# Revit family: Plum Fix_Toilet_Argent_Grace BTW Toilet S&P Trap UNI ENTRY
name_source: partatom
category: Plumbing Fixtures
revit_build: Autodesk Revit 2016 (Build: 20150220_1215(x64)
units: mm (PartAtom-declared; Revit-internal decimal feet)

## family parameters
Always vertical = Yes
Cut with Voids When Loaded = No
OmniClass Number = 23.45.05.21.11
OmniClass Title = Water Closets
Part Type = Normal
Room Calculation Point = No
Round Connector Dimension = Use Diameter
Shared = No
Work Plane-Based = No

## types (1)
- S-Trap  - Rear Water Entry
    Angle Offset = 0 mm  [stored 0 ft]
    Body Material = z_Argent_Ceramic White
    CW Connection = Yes
    CWFU = 0
    Cost = 0 $
    Description = Grace Back-To-Wall Toilet Suite
    Flush Material = z_Argent_Chrome
    HW Connection = No
    HWFU = 0
    Manufacturer = Argent
    Manufacturer_Overall Depth = 620 mm  [stored 2.03412 ft]
    Manufacturer_Overall Height = 795 mm  [stored 2.60827 ft]
    Manufacturer_Overall Width = 380 mm
    Manufacturer_Spec Code = 807601S4UB
    Manufacturer_URL__Product Specific = https://www.argentaust.com.au
    Model = 807601S4UB
    ModifiedIssue_ANZRS = 20190503 $
    Open Toilet Seat Visibility = No
    Toilet P Trap = Yes
    Toilet S Trap = No
    Toilet Seat Visibility = Yes
    Trap Angle = 0.00°
    Trap Offset = 170 mm
    Trap Offset Value = 170 mm
    Type Comments = S-Trap - Rear Water Entry
    URL = https://www.argentaust.com.au
    Vent Connection = No
    WFU = 0
    Waste Connection = Yes

note: [stored X ft] marks values corroborated as IEEE doubles in the binary element streams (Revit-internal decimal feet)

## geometry (parser evidence)
native form markers: Sweep x4
no freeform markers — native parametric forms only
